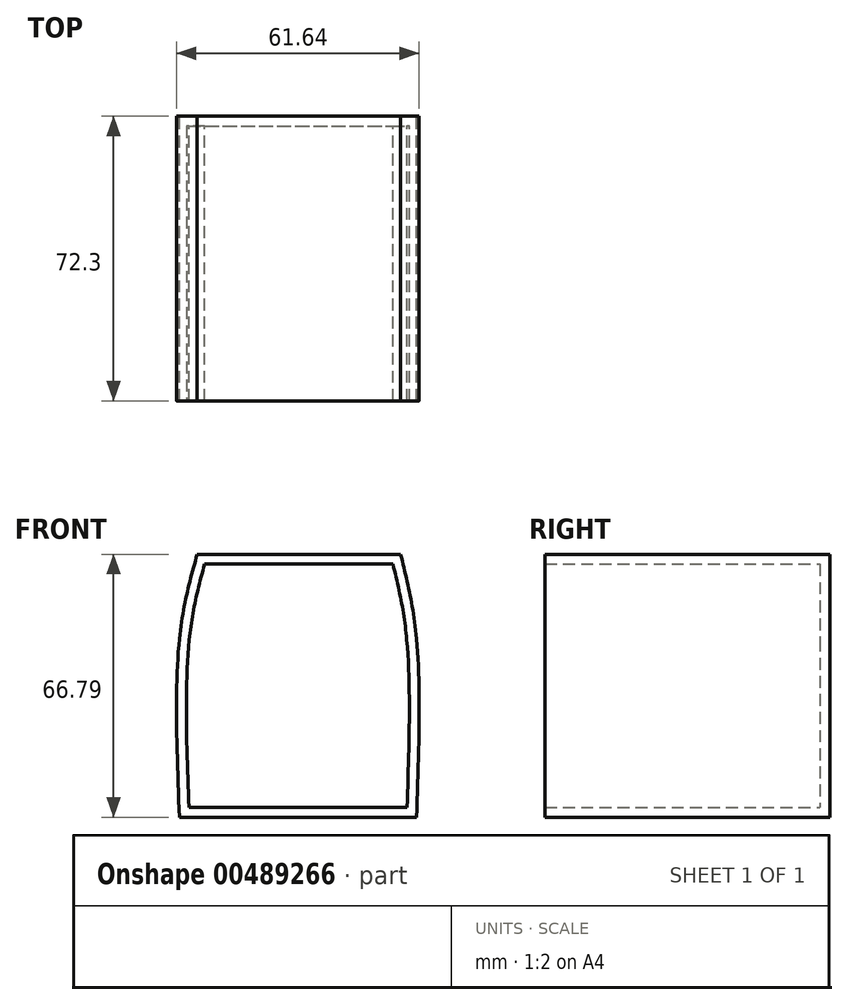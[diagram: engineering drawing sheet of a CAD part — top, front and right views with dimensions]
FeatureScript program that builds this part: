
annotation { "Feature Type Name" : "Feature", "Feature Type Description" : "" }
export const myFeature = defineFeature(function(context is Context, id is Id, definition is map)
    precondition{}
    {
        {
            var Q0;
            Q0=qCreatedBy(makeId("Front.planeOp"),FACE);
            var sketch = newSketch(context, id + "F0", { "sketchPlane" : qUnion([Q0])});
            skLineSegment(sketch, "E0.bottom", {"start": v(-29.1, 0) * mm, "end": v(31.14, 0) * mm});
            skLineSegment(sketch, "E0.top", {"start": v(-29.1, 45.34) * mm, "end": v(31.14, 45.34) * mm});
            skLineSegment(sketch, "E0.left", {"start": v(-29.1, 0) * mm, "end": v(-29.1, 45.34) * mm});
            skLineSegment(sketch, "E0.right", {"start": v(31.14, 0) * mm, "end": v(31.14, 45.34) * mm});
            skLineSegment(sketch, "E1", {"start": v(0, 66.8) * mm, "end": v(27.09, 66.8) * mm});
            skLineSegment(sketch, "E2", {"start": v(0, 66.8) * mm, "end": v(-21.6, 66.8) * mm});
            skLineSegment(sketch, "E3", {"start": v(-21.6, 66.8) * mm, "end": v(-24.59, 66.8) * mm});
            skFitSpline(sketch, "E4", {"points": [v(-24.59, 66.8) * mm, v(-29.1, 45.34) * mm, v(-29.1, 0) * mm], "startDerivative": vector(-13.26, -47.27) * mm, "endDerivative": vector(3.25, -84.1) * mm});
            skFitSpline(sketch, "E5", {"points": [v(27.09, 66.8) * mm, v(31.14, 45.34) * mm, v(31.14, 0) * mm], "startDerivative": vector(11.9, -47.37) * mm, "endDerivative": vector(-2.92, -84) * mm});
            skSolve(sketch);
        }
        {
            var Q0;
            {var subQ0=sQuery(id+"F0.wireOp",EDGE,"E0.left");Q0=makeQuery(id+"F0.imprint","IMPRINT",FACE,{"disambiguationData":[TD([[makeQuery(id+"F0.imprint","IMPRINT",EDGE,{"derivedFrom":subQ0}),1.0]])]});}
            var Q1;
            {var subQ0=sQuery(id+"F0.wireOp",EDGE,"E0.right");Q1=makeQuery(id+"F0.imprint","IMPRINT",FACE,{"disambiguationData":[TD([[makeQuery(id+"F0.imprint","IMPRINT",EDGE,{"derivedFrom":subQ0}),-1.0]])]});}
            var Q2;
            Q2=makeQuery(id+"F0.imprint","IMPRINT",FACE,{"disambiguationData":[TD([[makeQuery(id+"F0.imprint","IMPRINT",EDGE,{"derivedFrom":sQuery(id+"F0.wireOp",EDGE,"E0.bottom")}),1.0]])]});
            var Q3;
            {var subQ2=sQuery(id+"F0.wireOp",EDGE,"E0.top");Q3=makeQuery(id+"F0.imprint","IMPRINT",FACE,{"disambiguationData":[TD([[makeQuery(id+"F0.imprint","IMPRINT",EDGE,{"derivedFrom":subQ2}),1.0]])]});}
            extrude(context, id + "F1", {"entities" : qUnion([Q0, Q1, Q2, Q3]), "depth" : 72.3 * mm});
        }
        {
            var Q0;
            Q0=makeQuery(id+"F1.opExtrude","CAP_FACE",FACE,{"disambiguationData":[OSD([sQuery(id+"F0.wireOp",EDGE,"E0.bottom"),sQuery(id+"F0.wireOp",EDGE,"E1"),sQuery(id+"F0.wireOp",EDGE,"E2"),sQuery(id+"F0.wireOp",EDGE,"E3"),sQuery(id+"F0.wireOp",EDGE,"E4"),sQuery(id+"F0.wireOp",EDGE,"E5")])],"isStart":false});
            shell(context, id + "F2", {"entities" : qUnion([Q0]), "thickness" : 2.5 * mm});
        }
    });
